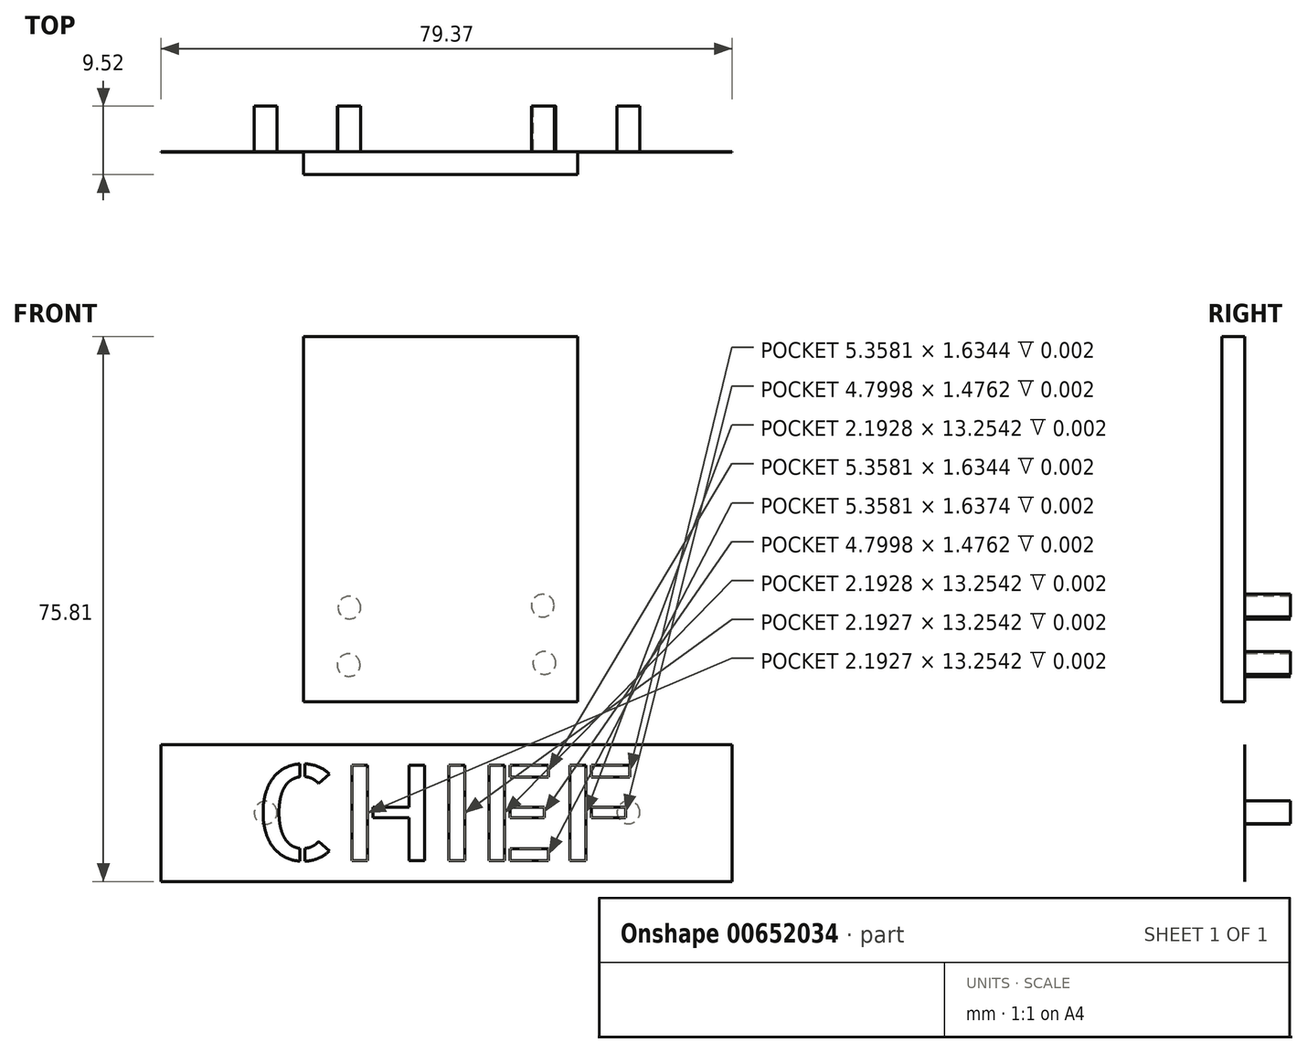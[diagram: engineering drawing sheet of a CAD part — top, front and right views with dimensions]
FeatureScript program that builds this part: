
annotation { "Feature Type Name" : "Feature", "Feature Type Description" : "" }
export const myFeature = defineFeature(function(context is Context, id is Id, definition is map)
    precondition{}
    {
        {
            var Q0;
            Q0=qCreatedBy(makeId("Front.planeOp"),FACE);
            var sketch = newSketch(context, id + "F0", { "sketchPlane" : qUnion([Q0])});
            skLineSegment(sketch, "E0", {"start": v(-92.65, -45.27) * mm, "end": v(-41.85, -45.27) * mm, "construction": true});
            skLineSegment(sketch, "E1.bottom", {"start": v(-80.75, -16.7) * mm, "end": v(-53.76, -16.7) * mm, "construction": true});
            skLineSegment(sketch, "E1.top", {"start": v(-80.75, -24.64) * mm, "end": v(-53.76, -24.64) * mm, "construction": true});
            skLineSegment(sketch, "E1.left", {"start": v(-80.75, -16.7) * mm, "end": v(-80.75, -24.64) * mm, "construction": true});
            skLineSegment(sketch, "E1.right", {"start": v(-53.76, -16.7) * mm, "end": v(-53.76, -24.64) * mm, "construction": true});
            skLineSegment(sketch, "E2", {"start": v(-67.25, -45.27) * mm, "end": v(-67.25, -16.7) * mm, "construction": true});
            skLineSegment(sketch, "E3.bottom", {"start": v(-106.94, -35.75) * mm, "end": v(-27.57, -35.75) * mm});
            skLineSegment(sketch, "E3.top", {"start": v(-106.94, -54.8) * mm, "end": v(-27.57, -54.8) * mm});
            skLineSegment(sketch, "E3.left", {"start": v(-106.94, -35.75) * mm, "end": v(-106.94, -54.8) * mm});
            skLineSegment(sketch, "E3.right", {"start": v(-27.57, -35.75) * mm, "end": v(-27.57, -54.8) * mm});
            skLineSegment(sketch, "E4.top", {"start": v(-109.09, -35.75) * mm, "end": v(-27.57, -35.75) * mm, "construction": true});
            skLineSegment(sketch, "E5.top", {"start": v(-87.25, -35.75) * mm, "end": v(-47.25, -35.75) * mm});
            skLineSegment(sketch, "E6.bottom", {"start": v(-93.45, -35.75) * mm, "end": v(-41.06, -35.75) * mm});
            skLineSegment(sketch, "E7.bottom", {"start": v(-87.15, 21.01) * mm, "end": v(-49.05, 21.01) * mm});
            skLineSegment(sketch, "E7.top", {"start": v(-87.15, -29.79) * mm, "end": v(-49.05, -29.79) * mm});
            skLineSegment(sketch, "E7.left", {"start": v(-87.15, 21.01) * mm, "end": v(-87.15, -29.79) * mm});
            skLineSegment(sketch, "E7.right", {"start": v(-49.05, 21.01) * mm, "end": v(-49.05, -29.79) * mm});
            skCircle(sketch, "E8", {"center": v(-80.75, -16.7) * mm, "radius": 1.59 * mm});
            skCircle(sketch, "E9", {"center": v(-53.87, -16.44) * mm, "radius": 1.59 * mm});
            skCircle(sketch, "E10", {"center": v(-53.65, -24.4) * mm, "radius": 1.59 * mm});
            skCircle(sketch, "E11", {"center": v(-80.84, -24.7) * mm, "radius": 1.59 * mm});
            skCircle(sketch, "E12", {"center": v(-41.96, -45.2) * mm, "radius": 1.59 * mm});
            skCircle(sketch, "E13", {"center": v(-92.4, -45.24) * mm, "radius": 1.59 * mm});
            skSolve(sketch);
        }
        {
            var Q0;
            Q0=makeQuery(id+"F0.imprint","IMPRINT",FACE,{"disambiguationData":[TD([[makeQuery(id+"F0.imprint","IMPRINT",EDGE,{"derivedFrom":sQuery(id+"F0.wireOp",EDGE,"E3.top")}),1.0]])]});
            var Q1;
            Q1=makeQuery(id+"F0.imprint","IMPRINT",FACE,{"disambiguationData":[TD([[makeQuery(id+"F0.imprint","IMPRINT",EDGE,{"derivedFrom":sQuery(id+"F0.wireOp",EDGE,"E13")}),1.0]])]});
            var Q2;
            Q2=makeQuery(id+"F0.imprint","IMPRINT",FACE,{"disambiguationData":[TD([[makeQuery(id+"F0.imprint","IMPRINT",EDGE,{"derivedFrom":sQuery(id+"F0.wireOp",EDGE,"E12")}),1.0]])]});
            extrude(context, id + "F1", {"entities" : qUnion([Q0, Q1, Q2]), "depth" : 1 / 203.2 * mm, "offsetDistance" : 25 * mm});
        }
        {
            var Q0;
            Q0=makeQuery(id+"F1.opExtrude","CAP_FACE",FACE,{"disambiguationData":[OSD([sQuery(id+"F0.wireOp",EDGE,"E3.bottom"),sQuery(id+"F0.wireOp",EDGE,"E3.top"),sQuery(id+"F0.wireOp",EDGE,"E3.left"),sQuery(id+"F0.wireOp",EDGE,"E3.right")])],"isStart":false});
            var sketch = newSketch(context, id + "F2", { "sketchPlane" : qUnion([Q0])});
            skText(sketch, "E14", { "text": "CHIEF", "fontName": "AllertaStencil-Regular.ttf"});
            skLineSegment(sketch, "E15", {"start": v(-82.05, -38.65) * mm, "end": v(-82.05, -35.75) * mm, "construction": true});
            skLineSegment(sketch, "E16", {"start": v(-82.35, -51.9) * mm, "end": v(-82.35, -54.8) * mm, "construction": true});
            skLineSegment(sketch, "E17", {"start": v(-94.05, -45.91) * mm, "end": v(-106.94, -45.91) * mm, "construction": true});
            skLineSegment(sketch, "E18", {"start": v(-40.46, -45.91) * mm, "end": v(-27.57, -45.91) * mm, "construction": true});
            const initialGuessF2  = {"E14": [-0.09416, -0.0519, 1, 0, 0.01326]};
            skSetInitialGuess(sketch, initialGuessF2);
            skSolve(sketch);
        }
        {
            var Q0;
            Q0 = qSketchRegion(id + "F2", true);
            extrude(context, id + "F3", {"entities" : qUnion([Q0]), "operationType" : NewBodyOperationType.REMOVE, "oppositeDirection" : true, "depth" : 1 / 406.4 * mm, "offsetDistance" : 25 * mm});
        }
        {
            var Q0;
            Q0=makeQuery(id+"F0.imprint","IMPRINT",FACE,{"disambiguationData":[TD([[makeQuery(id+"F0.imprint","IMPRINT",EDGE,{"derivedFrom":sQuery(id+"F0.wireOp",EDGE,"E7.bottom")}),-1.0]])]});
            var Q1;
            Q1=makeQuery(id+"F0.imprint","IMPRINT",FACE,{"disambiguationData":[TD([[makeQuery(id+"F0.imprint","IMPRINT",EDGE,{"derivedFrom":sQuery(id+"F0.wireOp",EDGE,"E8")}),1.0]])]});
            var Q2;
            Q2=makeQuery(id+"F0.imprint","IMPRINT",FACE,{"disambiguationData":[TD([[makeQuery(id+"F0.imprint","IMPRINT",EDGE,{"derivedFrom":sQuery(id+"F0.wireOp",EDGE,"E11")}),1.0]])]});
            var Q3;
            Q3=makeQuery(id+"F0.imprint","IMPRINT",FACE,{"disambiguationData":[TD([[makeQuery(id+"F0.imprint","IMPRINT",EDGE,{"derivedFrom":sQuery(id+"F0.wireOp",EDGE,"E9")}),1.0]])]});
            var Q4;
            Q4=makeQuery(id+"F0.imprint","IMPRINT",FACE,{"disambiguationData":[TD([[makeQuery(id+"F0.imprint","IMPRINT",EDGE,{"derivedFrom":sQuery(id+"F0.wireOp",EDGE,"E10")}),1.0]])]});
            extrude(context, id + "F4", {"entities" : qUnion([Q0, Q1, Q2, Q3, Q4]), "depth" : 3.17 * mm, "offsetDistance" : 25.4 * mm});
        }
        {
            var Q0;
            Q0=makeQuery(id+"F0.imprint","IMPRINT",FACE,{"disambiguationData":[TD([[makeQuery(id+"F0.imprint","IMPRINT",EDGE,{"derivedFrom":sQuery(id+"F0.wireOp",EDGE,"E9")}),1.0]])]});
            var Q1;
            Q1=makeQuery(id+"F0.imprint","IMPRINT",FACE,{"disambiguationData":[TD([[makeQuery(id+"F0.imprint","IMPRINT",EDGE,{"derivedFrom":sQuery(id+"F0.wireOp",EDGE,"E8")}),1.0]])]});
            var Q2;
            Q2=makeQuery(id+"F0.imprint","IMPRINT",FACE,{"disambiguationData":[TD([[makeQuery(id+"F0.imprint","IMPRINT",EDGE,{"derivedFrom":sQuery(id+"F0.wireOp",EDGE,"E11")}),1.0]])]});
            var Q3;
            Q3=makeQuery(id+"F0.imprint","IMPRINT",FACE,{"disambiguationData":[TD([[makeQuery(id+"F0.imprint","IMPRINT",EDGE,{"derivedFrom":sQuery(id+"F0.wireOp",EDGE,"E10")}),1.0]])]});
            extrude(context, id + "F5", {"entities" : qUnion([Q0, Q1, Q2, Q3]), "operationType" : NewBodyOperationType.ADD, "oppositeDirection" : true, "depth" : 6.35 * mm, "offsetDistance" : 25.4 * mm});
        }
        {
            var Q0;
            Q0=makeQuery(id+"F0.imprint","IMPRINT",FACE,{"disambiguationData":[TD([[makeQuery(id+"F0.imprint","IMPRINT",EDGE,{"derivedFrom":sQuery(id+"F0.wireOp",EDGE,"E12")}),1.0]])]});
            var Q1;
            Q1=makeQuery(id+"F0.imprint","IMPRINT",FACE,{"disambiguationData":[TD([[makeQuery(id+"F0.imprint","IMPRINT",EDGE,{"derivedFrom":sQuery(id+"F0.wireOp",EDGE,"E13")}),1.0]])]});
            var Q2;
            Q2=sQuery(id+"F0.wireOp",EDGE,"E13");
            var Q3;
            Q3=sQuery(id+"F0.wireOp",EDGE,"E12");
            extrude(context, id + "F6", {"entities" : qUnion([Q0, Q1]), "operationType" : NewBodyOperationType.ADD, "surfaceOperationType" : NewSurfaceOperationType.ADD, "surfaceEntities" : qUnion([Q2, Q3]), "oppositeDirection" : true, "depth" : 6.35 * mm, "offsetDistance" : 25.4 * mm});
        }
    });
